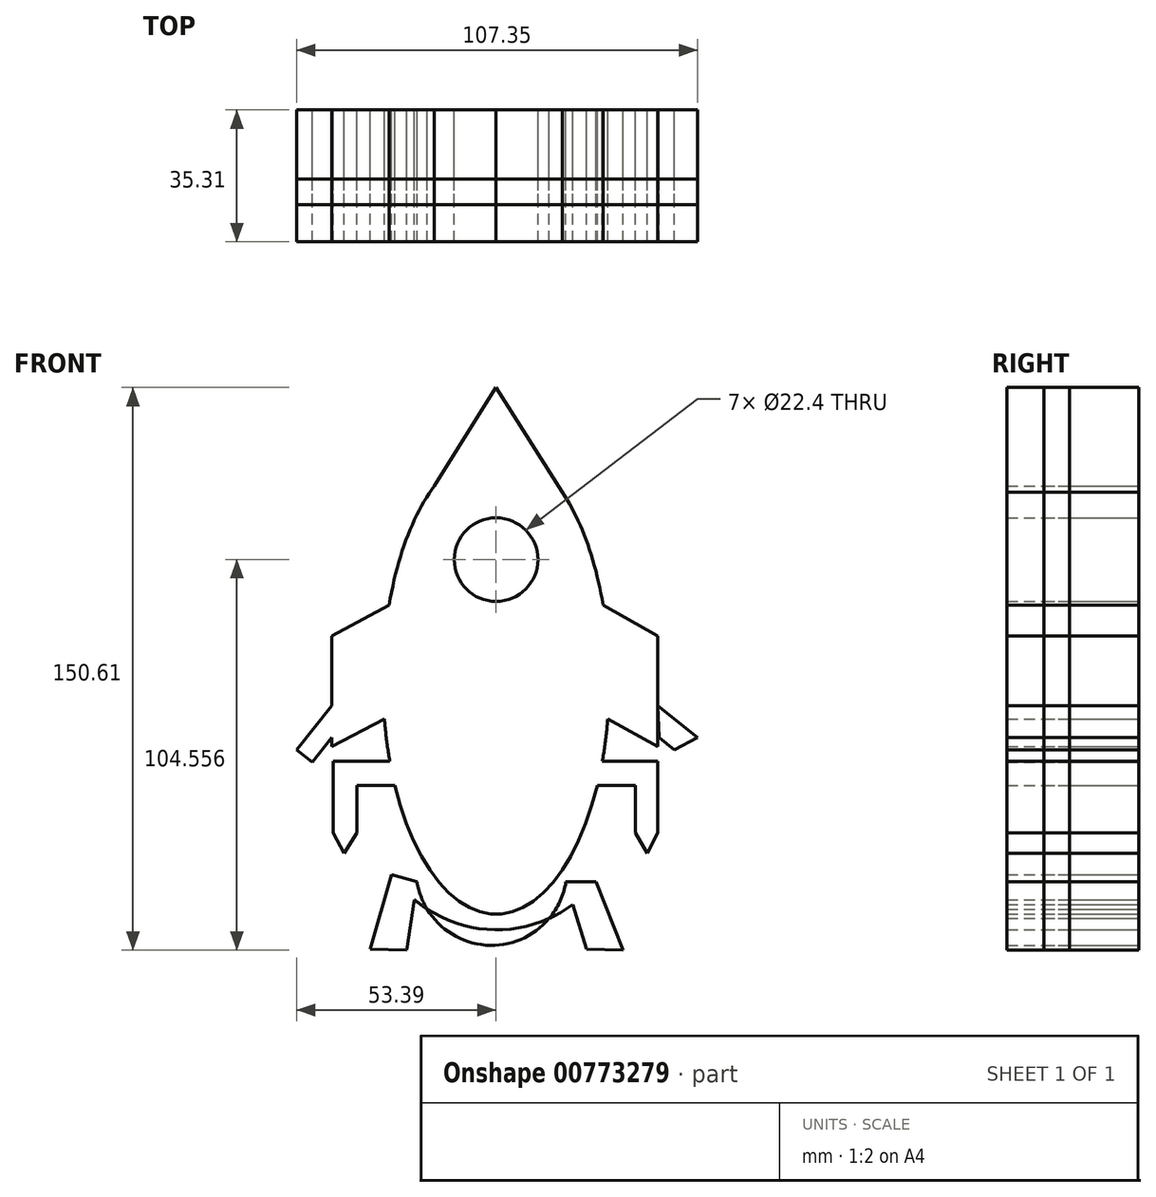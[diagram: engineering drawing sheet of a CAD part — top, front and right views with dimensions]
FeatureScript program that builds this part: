
annotation { "Feature Type Name" : "Feature", "Feature Type Description" : "" }
export const myFeature = defineFeature(function(context is Context, id is Id, definition is map)
    precondition{}
    {
        {
            var Q0;
            Q0=qCreatedBy(makeId("Front.planeOp"),FACE);
            var sketch = newSketch(context, id + "F0", { "sketchPlane" : qUnion([Q0])});
            skLineSegment(sketch, "E0", {"start": v(-33.74, -75.92) * mm, "end": v(-27.95, -55.94) * mm});
            skLineSegment(sketch, "E1", {"start": v(-27.95, -55.94) * mm, "end": v(-21.15, -57.9) * mm});
            skLineSegment(sketch, "E2", {"start": v(-21.15, -57.9) * mm, "end": v(-23.9, -76.2) * mm});
            skLineSegment(sketch, "E3", {"start": v(-23.9, -76.2) * mm, "end": v(-33.74, -75.92) * mm});
            skLineSegment(sketch, "E4", {"start": v(18.68, -57.9) * mm, "end": v(24.18, -75.92) * mm});
            skLineSegment(sketch, "E5", {"start": v(24.18, -75.92) * mm, "end": v(34.03, -76.2) * mm});
            skLineSegment(sketch, "E6", {"start": v(34.03, -76.2) * mm, "end": v(26.79, -57.9) * mm});
            skLineSegment(sketch, "E7", {"start": v(26.79, -57.9) * mm, "end": v(18.68, -57.9) * mm});
            skArc(sketch, "E8", {"start": v(-27.95, -55.94) * mm, "mid": v(-1.08, -70.7) * mm, "end": v(26.79, -57.9) * mm});
            skArc(sketch, "E9", {"start": v(-21.15, -57.9) * mm, "mid": v(-1.23, -74.89) * mm, "end": v(18.68, -57.9) * mm});
            skPoint(sketch, "E10.startSnap0", {"position": v(31.7, -1.15) * mm});
            skEllipse(sketch, "E11", {"center": v(0, -4.18) * mm, "majorRadius": 62.37 * mm, "minorRadius": 30.3 * mm, "majorAxis": v(0, 1)});
            skLineSegment(sketch, "E12", {"start": v(17.72, 46.41) * mm, "end": v(0, 74.4) * mm});
            skLineSegment(sketch, "E13", {"start": v(0, 74.4) * mm, "end": v(-16.52, 48.1) * mm});
            skCircle(sketch, "E14", {"center": v(0, 28.35) * mm, "radius": 11.2 * mm});
            skCircle(sketch, "E15", {"center": v(0, 28.35) * mm, "radius": 6.3 * mm});
            skLineSegment(sketch, "E16", {"start": v(-28.46, -25.56) * mm, "end": v(-43.6, -25.56) * mm});
            skLineSegment(sketch, "E17", {"start": v(-43.6, -25.56) * mm, "end": v(-43.6, -44.76) * mm});
            skLineSegment(sketch, "E18", {"start": v(-43.6, -44.76) * mm, "end": v(-40.73, -50.23) * mm});
            skLineSegment(sketch, "E19", {"start": v(-40.73, -50.23) * mm, "end": v(-37.27, -44.76) * mm});
            skLineSegment(sketch, "E20", {"start": v(-37.27, -44.76) * mm, "end": v(-37.27, -32.1) * mm});
            skLineSegment(sketch, "E21", {"start": v(-37.27, -32.1) * mm, "end": v(-27.09, -32.1) * mm});
            skLineSegment(sketch, "E22", {"start": v(28.46, -25.56) * mm, "end": v(43.32, -25.56) * mm});
            skLineSegment(sketch, "E23", {"start": v(43.32, -25.56) * mm, "end": v(43.32, -44.76) * mm});
            skLineSegment(sketch, "E24", {"start": v(43.32, -44.76) * mm, "end": v(40.44, -50.23) * mm});
            skLineSegment(sketch, "E25", {"start": v(40.44, -50.23) * mm, "end": v(37.27, -44.76) * mm});
            skLineSegment(sketch, "E26", {"start": v(37.27, -44.76) * mm, "end": v(37.27, -32.1) * mm});
            skLineSegment(sketch, "E27", {"start": v(37.27, -32.1) * mm, "end": v(26.79, -32.1) * mm});
            skLineSegment(sketch, "E28", {"start": v(-28.63, 16.22) * mm, "end": v(-43.97, 7.91) * mm});
            skLineSegment(sketch, "E29", {"start": v(-43.97, 7.91) * mm, "end": v(-43.97, -21.74) * mm});
            skLineSegment(sketch, "E30", {"start": v(-43.97, -21.74) * mm, "end": v(-29.9, -14.27) * mm});
            skLineSegment(sketch, "E31", {"start": v(28.63, 16.22) * mm, "end": v(43.32, 7.91) * mm});
            skLineSegment(sketch, "E32", {"start": v(43.32, 7.91) * mm, "end": v(43.32, -21.74) * mm});
            skLineSegment(sketch, "E33", {"start": v(43.32, -21.74) * mm, "end": v(29.9, -14.27) * mm});
            skLineSegment(sketch, "E34", {"start": v(-43.97, -10.8) * mm, "end": v(-53.4, -22.6) * mm});
            skLineSegment(sketch, "E35", {"start": v(-53.4, -22.6) * mm, "end": v(-49.25, -25.9) * mm});
            skLineSegment(sketch, "E36", {"start": v(-49.25, -25.9) * mm, "end": v(-43.97, -19.3) * mm});
            skLineSegment(sketch, "E37", {"start": v(43.32, -10.8) * mm, "end": v(53.96, -19.3) * mm});
            skPoint(sketch, "E37.startSnap0", {"position": v(43.32, -6.91) * mm});
            skLineSegment(sketch, "E38", {"start": v(53.96, -19.3) * mm, "end": v(47.73, -22.6) * mm});
            skLineSegment(sketch, "E39", {"start": v(47.73, -22.6) * mm, "end": v(43.6, -19.3) * mm});
            skLineSegment(sketch, "E40", {"start": v(43.6, -19.3) * mm, "end": v(43.32, -10.8) * mm});
            skLineSegment(sketch, "E41", {"start": v(-43.97, -19.3) * mm, "end": v(-43.97, -10.8) * mm});
            skSolve(sketch);
        }
        {
            var Q0;
            Q0 = qSketchRegion(id + "F0", true);
            extrude(context, id + "F1", {"entities" : qUnion([Q0]), "depth" : 18.54 * mm, "offsetDistance" : 25.4 * mm});
        }
        {
            var Q0;
            Q0 = qSketchRegion(id + "F0", true);
            extrude(context, id + "F2", {"entities" : qUnion([Q0]), "depth" : 35.3 * mm, "offsetDistance" : 25.4 * mm});
        }
        {
            var Q0;
            Q0 = qSketchRegion(id + "F0", true);
            extrude(context, id + "F3", {"entities" : qUnion([Q0]), "depth" : 25.4 * mm, "offsetDistance" : 25.4 * mm});
        }
        {
            var Q0;
            Q0 = qSketchRegion(id + "F0", true);
            extrude(context, id + "F4", {"entities" : qUnion([Q0]), "depth" : 25.4 * mm, "offsetDistance" : 25.4 * mm});
        }
        {
            var Q0;
            Q0 = qSketchRegion(id + "F0", true);
            extrude(context, id + "F5", {"entities" : qUnion([Q0]), "depth" : 25.4 * mm, "offsetDistance" : 25.4 * mm});
        }
        {
            var Q0;
            Q0 = qSketchRegion(id + "F0", true);
            extrude(context, id + "F6", {"entities" : qUnion([Q0]), "depth" : 25.4 * mm, "offsetDistance" : 25.4 * mm});
        }
        {
            var Q0;
            Q0 = qSketchRegion(id + "F0", true);
            extrude(context, id + "F7", {"entities" : qUnion([Q0]), "depth" : 25.4 * mm, "offsetDistance" : 25.4 * mm});
        }
    });
